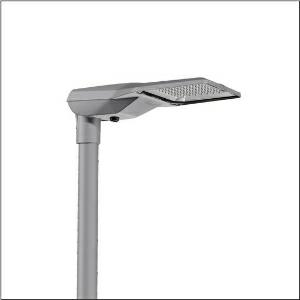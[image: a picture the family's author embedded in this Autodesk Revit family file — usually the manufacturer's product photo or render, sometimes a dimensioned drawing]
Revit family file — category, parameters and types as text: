
# Revit family: streetlight_sl_21_iq_midi___p0_5a_5xe3v31u08nb_f0ed
name_source: partatom
category: Lighting Fixtures
units: mm (PartAtom-declared; Revit-internal decimal feet)

## family parameters
Cut with Voids When Loaded = No
Host = Face
Light Source = No
Part Type = Normal
Room Calculation Point = No
Round Connector Dimension = Use Diameter
Shared = No

## types (1)
- --- (1 x LED, 21180 lm, 136.6 W, 3000K)
    Apparent Load = 137 VA
    CIE Flux Codes = 37 73 96 100 100
    Color Rendering = 70
    Color Temperature = 3000K
    Default Elevation = 1800 mm
    Description = Streetlight SL 21 iQ midi, mast luminaire, primary light control with lens, of PMMA, primary optical cover: cover, of toughened safety glass, transparent, light distribution: P0.5a, light emission: direct distribution, primary light characteristic: asymmetric, installation type: post-top, side-entry, LED, High Power LED, rated luminous flux: 21.180lm, luminous efficacy: 155lm/W, light colour: 730, colour temperature: 3000K, control gear: iQ-Street Remote, D4i with power reduction, control: pre-setting: logarithmic dimming characteristic, Street-Remote, Auto-Match, Temp-Guard, Lumen-Switch, Night-Set, Smart-Wire, Light-Fading, Desk-Remote (wireless, voltage-free reading and setting of iQ features in the workshop via application-optimized NFC function/RFID function), optimised constant luminous flux control (CLO 2.0), mains connection: 230..240V, AC, 50/60Hz, start of lifetime: 137W, end of service life: 144W, reduction: 61W, luminaire housing, of diecast aluminium, powder-coated, SITECO metallic grey (DB 702S), corrosivity category C5 high according to DIN EN ISO 12944, please order mast flange separately, inclination adjustable: 0°, 5°, 10°, 15°, sealing non-destructively replaceable, multi-level sealing system, length: 644mm, width: 335mm, height: 110mm, mast flange for spigot size: 42mm (side-entry): 5XC10008XM4, 60/48mm (side-entry/post-top): 5XC10108XM2, 76/60mm (side-entry/post-top): 5XC10108XM1, mounting height: 4..8m, Smart Interface below, protection rating (complete): IP66, insulation class (complete): insulation class II (safety insulation), certification: CE, ENEC, ENEC+, VDE, impact resistance: IK10, permissible operating ambient temperature for outdoor applications: -40..+50°C, standard-compliant lighting for roads and squares, packaging unit: 1 piece

Light Distribution: P0.5a
    Height = 111 mm
    Lamp = 1 x LED
    Lamp Light Flux = 21180 lm
    Lamp Power = 136.6 W
    Lamp count = 1
    Length = 644 mm
    Luminous efficacy = 155 lm/W
    Manufacturer = Siteco
    ModVariant = No
    Model = 5XE3V31U08NB
    Number of Poles = 1
    OnlyDefault = Yes
    Power Factor = 1
    Product Name = Streetlight SL 21 iQ midi | P0.5a
    Product group = mast luminaire | pylon top
    ProductGroupID = 6100
    Protection Class = Protection class II
    Protection Degree = IP 66
    RLX_Detail_Level = 1
    RLX_Emergency_Light_Flux = 0 lm
    RLX_Emergency_Type = 0
    RLX_Emergency_Type_DB = No
    RlxData = <blob elided: 91221 chars, md5=a26575c7>
    Socket = socket
    Standby Power = 0 W
    System Light Flux = 21180 lm
    System Power = 137 W
    Type Comments = factory setting: luminous flux: 100 % | dim-lin: 254 | 733 mA
    Type Image = l_1004300.jpg
    URL = http://relux.com
    VarID = @adj_077091
    Voltage = 0 V
    Weight = 0.00 kg
    Width = 336 mm

## geometry (parser evidence)
native form markers: Blend x4, Sweep x14
no freeform markers — native parametric forms only
